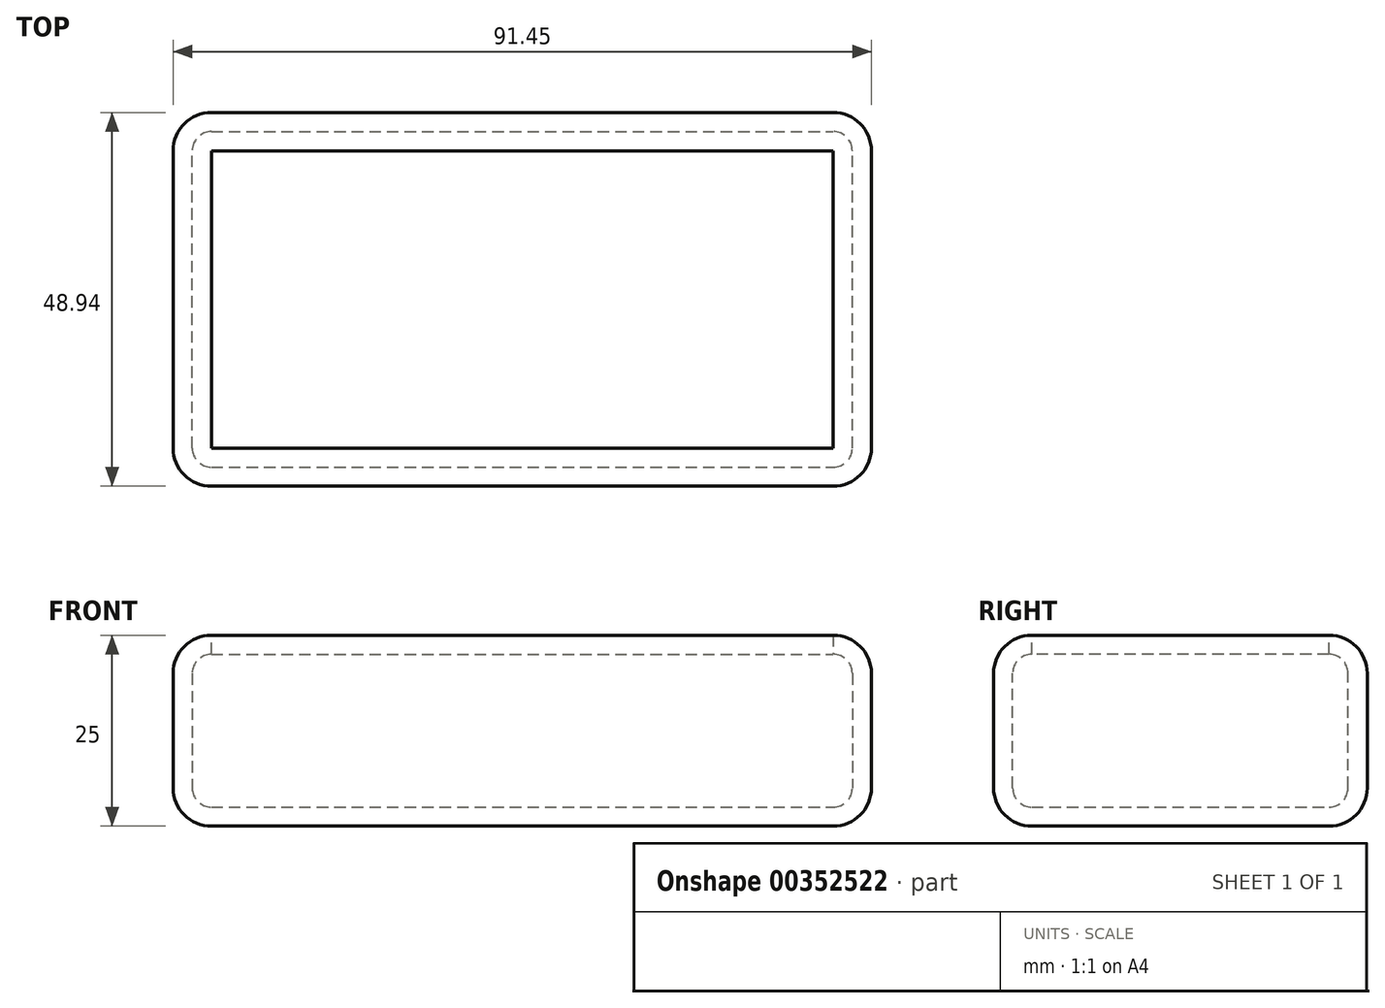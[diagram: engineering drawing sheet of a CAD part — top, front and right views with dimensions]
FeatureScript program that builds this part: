
annotation { "Feature Type Name" : "Feature", "Feature Type Description" : "" }
export const myFeature = defineFeature(function(context is Context, id is Id, definition is map)
    precondition{}
    {
        {
            var Q0;
            Q0=qCreatedBy(makeId("Top.planeOp"),FACE);
            var sketch = newSketch(context, id + "F0", { "sketchPlane" : qUnion([Q0])});
            skLineSegment(sketch, "E0.bottom", {"start": v(-44.9, 23.87) * mm, "end": v(46.55, 23.87) * mm});
            skLineSegment(sketch, "E0.top", {"start": v(-44.9, -25.07) * mm, "end": v(46.55, -25.07) * mm});
            skLineSegment(sketch, "E0.left", {"start": v(-44.9, 23.87) * mm, "end": v(-44.9, -25.07) * mm});
            skLineSegment(sketch, "E0.right", {"start": v(46.55, 23.87) * mm, "end": v(46.55, -25.07) * mm});
            skSolve(sketch);
        }
        {
            var Q0;
            Q0 = qSketchRegion(id + "F0", true);
            extrude(context, id + "F1", {"entities" : qUnion([Q0]), "endBound" : BoundingType.SYMMETRIC, "depth" : 25 * mm});
        }
        {
            var Q0;
            Q0=makeQuery(id+"F1.opExtrude","SWEPT_EDGE",EDGE,{"disambiguationData":[OSD([sQuery(id+"F0.wireOp",EDGE,"E0.bottom"),sQuery(id+"F0.wireOp",EDGE,"E0.left")])]});
            fillet(context, id + "F2", {"entities" : qUnion([Q0]), "radius" : 5 * mm, "tangentPropagation" : true, "allowEdgeOverflow" : false});
        }
        {
            var Q0;
            Q0=makeQuery(id+"F1.opExtrude","SWEPT_EDGE",EDGE,{"disambiguationData":[OSD([sQuery(id+"F0.wireOp",EDGE,"E0.top"),sQuery(id+"F0.wireOp",EDGE,"E0.left")])]});
            var Q1;
            Q1=makeQuery(id+"F1.opExtrude","CAP_FACE",FACE,{"disambiguationData":[OSD([sQuery(id+"F0.wireOp",EDGE,"E0.bottom"),sQuery(id+"F0.wireOp",EDGE,"E0.top"),sQuery(id+"F0.wireOp",EDGE,"E0.left"),sQuery(id+"F0.wireOp",EDGE,"E0.right")])],"isStart":true});
            fillet(context, id + "F3", {"entities" : qUnion([Q0, Q1]), "radius" : 5 * mm, "tangentPropagation" : true, "allowEdgeOverflow" : false});
        }
        {
            var Q0;
            Q0=makeQuery(id+"F1.opExtrude","SWEPT_EDGE",EDGE,{"disambiguationData":[OSD([sQuery(id+"F0.wireOp",EDGE,"E0.bottom"),sQuery(id+"F0.wireOp",EDGE,"E0.right")])]});
            var Q1;
            Q1=makeQuery(id+"F1.opExtrude","SWEPT_FACE",FACE,{"disambiguationData":[OSD([sQuery(id+"F0.wireOp",EDGE,"E0.right")])]});
            var Q2;
            Q2=makeQuery(id+"F1.opExtrude","CAP_EDGE",EDGE,{"disambiguationData":[OSD([sQuery(id+"F0.wireOp",EDGE,"E0.bottom")])],"isStart":false});
            fillet(context, id + "F4", {"entities" : qUnion([Q0, Q1, Q2]), "radius" : 5 * mm, "tangentPropagation" : true, "allowEdgeOverflow" : false});
        }
        {
            var Q0;
            Q0=makeQuery(id+"F1.opExtrude","CAP_FACE",FACE,{"disambiguationData":[OSD([sQuery(id+"F0.wireOp",EDGE,"E0.bottom"),sQuery(id+"F0.wireOp",EDGE,"E0.top"),sQuery(id+"F0.wireOp",EDGE,"E0.left"),sQuery(id+"F0.wireOp",EDGE,"E0.right")])],"isStart":false});
            shell(context, id + "F5", {"entities" : qUnion([Q0]), "thickness" : 2.5 * mm});
        }
    });
